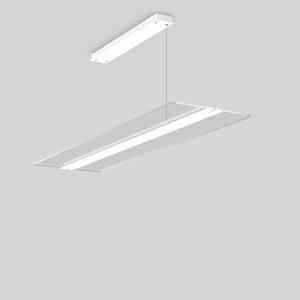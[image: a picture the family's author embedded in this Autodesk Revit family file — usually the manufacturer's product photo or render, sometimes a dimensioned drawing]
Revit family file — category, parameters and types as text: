
# Revit family: twindot_s_312263_002_1_76_6509
name_source: partatom
category: Lighting Fixtures
units: mm (PartAtom-declared; Revit-internal decimal feet)

## family parameters
Cut with Voids When Loaded = No
Host = Face
Light Source = No
Part Type = Normal
Room Calculation Point = No
Round Connector Dimension = Use Diameter
Shared = No

## types (1)
- TWINDOT S (1 x LED Modul 840, 6500 lm, 4000)
    Apparent Load = 54 VA
    CIE Flux Codes = 47 77 94 55 100
    Color Rendering = 80
    Color Temperature = 4000
    Default Elevation = 1800 mm
    Description = Series: TWINDOT S
LED pendant luminaire with extremely flat and frameless appearance. Middle bar made of aluminium extrusion profile, powder-coated. Transparent light guide made of UV-resistant acrylic glass (PMMA) with TWINDOT prismatic. Light control with perfectly glare-free TWINDOT technology for pleasantly gentle light with soft shadows. Even and wide indirect and direct light distribution. Direct 55%, indirect 45% light emission. 4-point steel cable suspension, steplessly adjustable. Converter integrated in the canopy (powder-coated white). Power supply through suspension cable. 
Colour: traffic white, matt (RAL 9016)
Length: 1200 mm
Width: 350 mm
Height: 20 mm
Suspension length: 500-1200 mm
Lamp: LED
Socket: without socket
Colour temperature: 4000K
Colour rendering index (CRI): 80
System power: 54 W
Rated luminous flux: 6500 lm
Luminous efficiency: 120 lm/W
Control gear: Converter, dimmable, DALI
Protection class: I
Type of protection: IP 20
    Height = 20 mm  [stored 0.0656168 ft]
    Lamp = 1 x LED Modul 840
    Lamp Light Flux = 6500 lm
    Lamp count = 1
    Length = 1200 mm
    Lifetime = 50000 h
    Luminous efficacy = 120 lm/W
    Manufacturer = RZB
    ModVariant = No
    Model = 312263.002.1.76
    Mounting Place = Ceiling
    Mounting Type = Pendant
    Number of Poles = 1
    OnlyDefault = Yes
    Power Factor = 1
    Product Name = TWINDOT S
    Product group = Pendant modular luminaires
    ProductGroupID = 906
    Protection Class = Protection class I
    Protection Degree = IP 20
    RLX_Detail_Level = 1
    RLX_Emergency_Light_Flux = 0 lm
    RLX_Emergency_Type = 0
    RLX_Emergency_Type_DB = No
    RlxData = <blob elided: 35321 chars, md5=8ffa9c74>
    Socket = socket
    Standby Power = 0 W
    System Light Flux = 6500 lm
    System Power = 54 W
    Type Comments = Product without accessories
    Type Image = 312263.002.jpg
    URL = http://relux.com
    VarID = ---
    Voltage = 230 V
    Voltage Range = 220-240 V
    Weight = 0.00 kg
    Width = 350 mm

note: [stored X ft] marks values corroborated as IEEE doubles in the binary element streams (Revit-internal decimal feet)

## geometry (parser evidence)
native form markers: Blend x4, Sweep x12
no freeform markers — native parametric forms only
